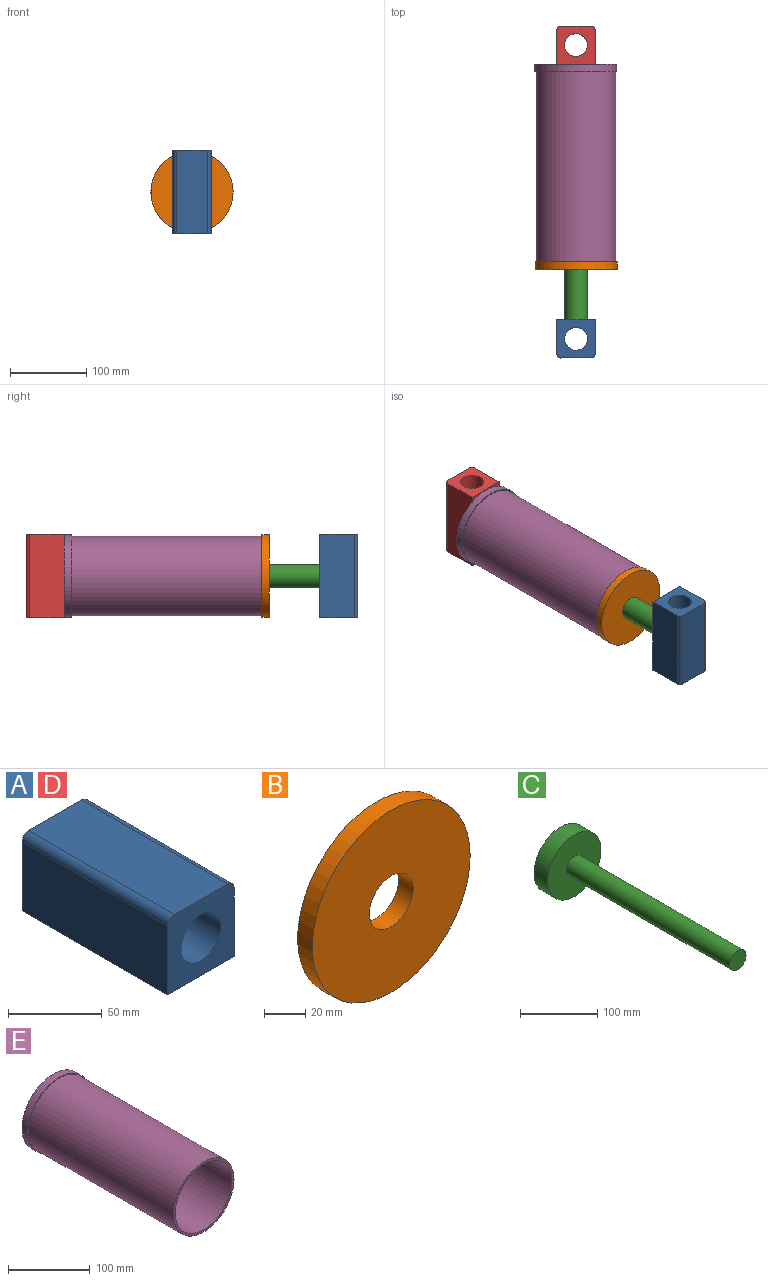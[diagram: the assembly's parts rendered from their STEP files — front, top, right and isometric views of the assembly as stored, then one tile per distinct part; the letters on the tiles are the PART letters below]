
ASSEMBLY  parts=5 mates=4
PART A: 9 faces, bbox 50x110x50 mm
  f0: plane 110x45mm, normal (-1,0,0), area 4950mm2, adj f1,f5,f6,f8
  f1: plane 110x50mm, normal (0,0,-1), area 5500mm2, adj f0,f2,f5,f6
  f2: plane 110x45mm, normal (1,0,0), area 4950mm2, adj f1,f5,f6,f7
  f3: cylinder r=15mm len=110mm, axis (0,1,0), area 10367.3mm2, adj f5,f6
  f4: plane 110x40mm, normal (0,0,1), area 4400mm2, adj f5,f6,f7,f8
  f5: plane 50x50mm, normal (0,-1,0), area 1782.4mm2, adj f0,f1,f2,f3,f4,f7,f8
  f6: plane 50x50mm, normal (0,1,0), area 1782.4mm2, adj f0,f1,f2,f3,f4,f7,f8
  f7: cylinder r=5mm len=110mm, axis (0,1,0), area 863.9mm2, adj f2,f4,f5,f6
  f8: cylinder r=5mm len=110mm, axis (0,-1,0), area 863.9mm2, adj f0,f4,f5,f6
PART B: 4 faces, bbox 108x10x108 mm
  f0: cylinder r=15mm len=30mm, axis (0,1,0), area 942.5mm2, adj f2,f3
  f1: cylinder r=54mm len=108mm, axis (0,1,0), area 3392.9mm2, adj f2,f3
  f2: plane 108x108mm, normal (0,-1,0), area 8454mm2, adj f0,f1
  f3: plane 108x108mm, normal (0,1,0), area 8454mm2, adj f0,f1
PART C: 5 faces, bbox 98x325x98 mm
  f0: cylinder r=15mm len=300mm, axis (0,1,0), area 28274.3mm2, adj f1,f4
  f1: plane 30x30mm, normal (0,-1,0), area 706.9mm2, adj f0
  f2: cylinder r=49mm len=98mm, axis (0,-1,0), area 7696.9mm2, adj f3,f4
  f3: plane 98x98mm, normal (0,1,0), area 7543mm2, adj f2
  f4: plane 98x98mm, normal (0,-1,0), area 6836.1mm2, adj f0,f2
PART D: same geometry as A
PART E: 7 faces, bbox 108x260x108 mm
  f0: cylinder r=49mm len=250mm, axis (0,1,0), area 76969mm2, adj f2,f6
  f1: cylinder r=52.5mm len=250mm, axis (0,1,0), area 82466.8mm2, adj f2,f3
  f2: plane 105x105mm, normal (0,-1,0), area 1116.1mm2, adj f0,f1
  f3: plane 108x108mm, normal (0,-1,0), area 501.9mm2, adj f1,f5
  f4: plane 108x108mm, normal (0,1,0), area 9160.9mm2, adj f5
  f5: cylinder r=54mm len=108mm, axis (0,-1,0), area 3392.9mm2, adj f3,f4
  f6: plane 98x98mm, normal (0,-1,0), area 7543mm2, adj f0
PLACE A rot(axis=(1,0,0),90deg) t=(-77.36,-332.66,80.49)mm
PLACE B rot(axis=(0,-1,0),0deg) t=(-31.59,-242.2,-15.76)mm
PLACE C rot(axis=(0,-1,0),0deg) t=(-44.27,-18.48,2.5)mm
PLACE D rot(axis=(0,0.71,0.71),180deg) t=(-111.52,31.98,80.49)mm
PLACE E t=(-59.74,7.8,-15.33)mm
MATE fastened D.f1 <-> E.f0  axis (0,-1,0) through (-94.44,17.8,25.49)mm
MATE fastened A.f1 <-> C.f0  axis (0,1,0) through (-94.44,-318.48,25.49)mm
MATE fastened E.f0 <-> B.f0  axis (0,1,0) through (-94.44,-242.2,25.49)mm
MATE slider C.f0 <-> E.f0  axis (0,-1,0) through (-94.44,-18.48,25.49)mm
